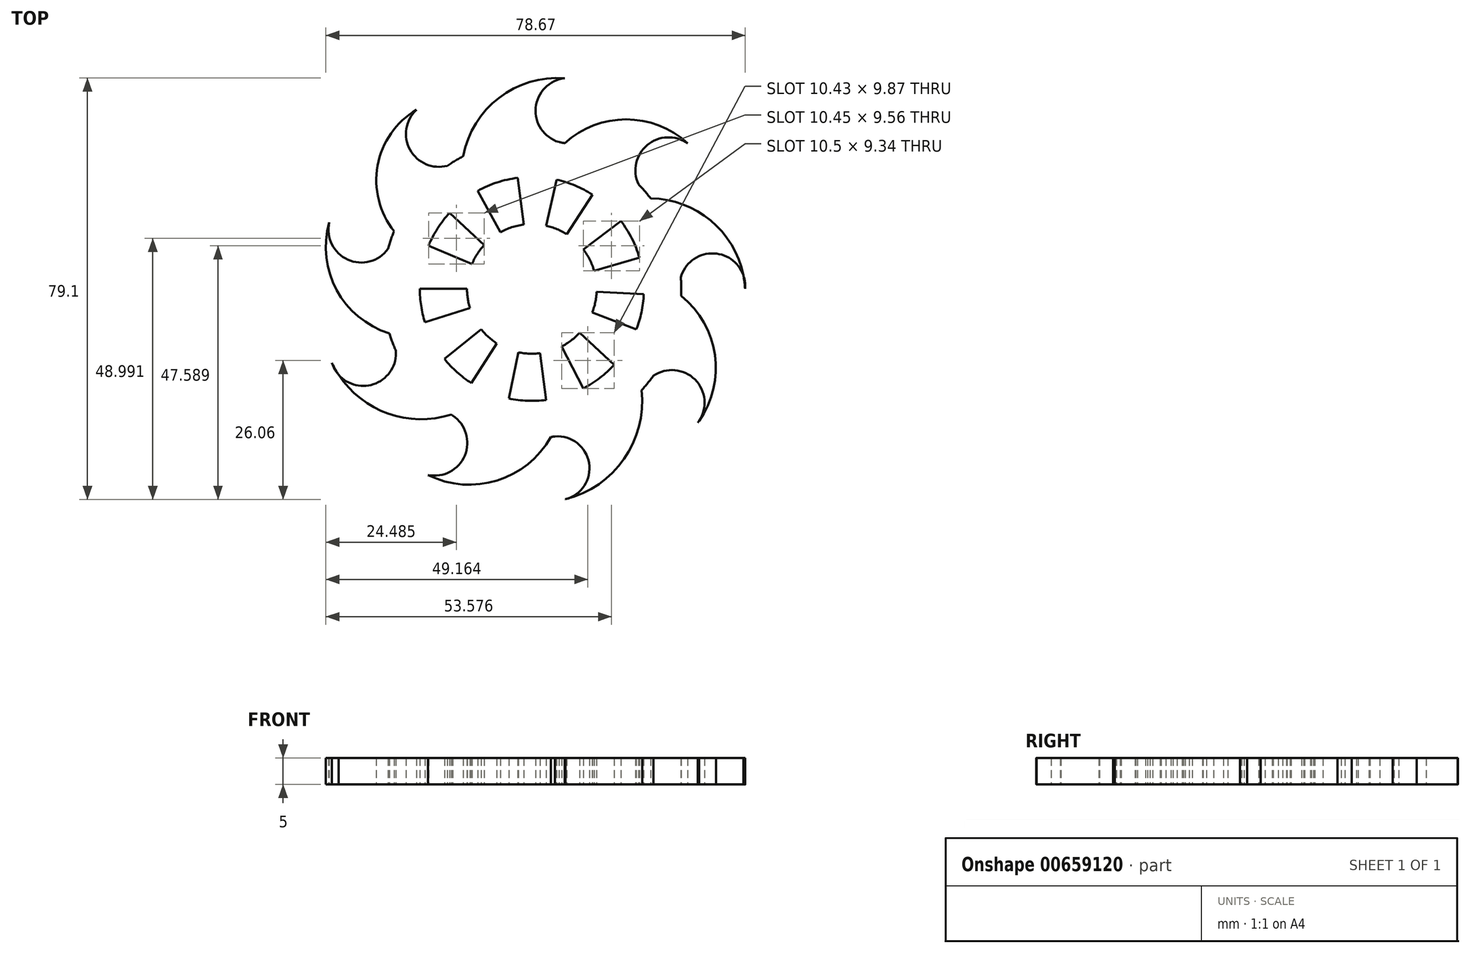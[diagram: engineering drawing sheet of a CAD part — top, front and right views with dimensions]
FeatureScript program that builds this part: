
annotation { "Feature Type Name" : "Feature", "Feature Type Description" : "" }
export const myFeature = defineFeature(function(context is Context, id is Id, definition is map)
    precondition{}
    {
        {
            var Q0;
            Q0=qCreatedBy(makeId("Top.planeOp"),FACE);
            var sketch = newSketch(context, id + "F0", { "sketchPlane" : qUnion([Q0])});
            skCircle(sketch, "E0", {"center": v(0, 0) * mm, "radius": 28.02 * mm});
            skCircle(sketch, "E1.cCircle", {"center": v(0, 0) * mm, "radius": 28.02 * mm, "construction": true});
            skLineSegment(sketch, "E1.0", {"start": v(20.6, -19) * mm, "end": v(3.57, -27.8) * mm});
            skLineSegment(sketch, "E1.1", {"start": v(3.57, -27.8) * mm, "end": v(-15.14, -23.58) * mm});
            skLineSegment(sketch, "E1.2", {"start": v(-15.14, -23.58) * mm, "end": v(-26.75, -8.34) * mm});
            skLineSegment(sketch, "E1.3", {"start": v(-26.75, -8.34) * mm, "end": v(-25.85, 10.8) * mm});
            skLineSegment(sketch, "E1.4", {"start": v(-25.85, 10.8) * mm, "end": v(-12.86, 24.9) * mm});
            skLineSegment(sketch, "E1.5", {"start": v(-12.86, 24.9) * mm, "end": v(6.16, 27.34) * mm});
            skLineSegment(sketch, "E1.6", {"start": v(6.16, 27.34) * mm, "end": v(22.29, 16.99) * mm});
            skLineSegment(sketch, "E1.7", {"start": v(22.29, 16.99) * mm, "end": v(28, -1.32) * mm});
            skLineSegment(sketch, "E1.8", {"start": v(28, -1.32) * mm, "end": v(20.6, -19) * mm});
            skLineSegment(sketch, "E2", {"start": v(6.16, 27.34) * mm, "end": v(0.33, 1.46) * mm});
            skLineSegment(sketch, "E3", {"start": v(1.2, 0.9) * mm, "end": v(22.29, 16.99) * mm});
            skLineSegment(sketch, "E4", {"start": v(1.5, -0.07) * mm, "end": v(28, -1.32) * mm});
            skLineSegment(sketch, "E5", {"start": v(1.1, -1.02) * mm, "end": v(20.6, -19) * mm});
            skLineSegment(sketch, "E6", {"start": v(0.2, -1.49) * mm, "end": v(3.57, -27.8) * mm});
            skLineSegment(sketch, "E7", {"start": v(-0.81, -1.26) * mm, "end": v(-15.14, -23.58) * mm});
            skLineSegment(sketch, "E8", {"start": v(-1.43, -0.45) * mm, "end": v(-26.75, -8.34) * mm});
            skLineSegment(sketch, "E9", {"start": v(-1.38, 0.58) * mm, "end": v(-25.85, 10.8) * mm});
            skLineSegment(sketch, "E10", {"start": v(-0.73, 1.31) * mm, "end": v(-13.44, 24.27) * mm});
            skArc(sketch, "E11", {"start": v(-21.68, 33.62) * mm, "mid": v(-22.37, 33.16) * mm, "end": v(-23.06, 32.69) * mm});
            skArc(sketch, "E12", {"start": v(29.2, 27.34) * mm, "mid": v(17.68, 31.81) * mm, "end": v(6.16, 27.34) * mm});
            skArc(sketch, "E13", {"start": v(29.2, 27.34) * mm, "mid": v(20.47, 25.68) * mm, "end": v(22.29, 16.99) * mm});
            skArc(sketch, "E14", {"start": v(40, 0) * mm, "mid": v(34.5, 11.98) * mm, "end": v(22.29, 16.99) * mm});
            skArc(sketch, "E15", {"start": v(40, 0) * mm, "mid": v(33.2, 6.63) * mm, "end": v(28, -1.32) * mm});
            skArc(sketch, "E16", {"start": v(31.11, -25.14) * mm, "mid": v(34.38, -12.6) * mm, "end": v(28, -1.32) * mm});
            skArc(sketch, "E17", {"start": v(31.11, -25.14) * mm, "mid": v(29.36, -16.07) * mm, "end": v(20.6, -19) * mm});
            skArc(sketch, "E18", {"start": v(6.16, -39.52) * mm, "mid": v(17.24, -31.98) * mm, "end": v(20.6, -19) * mm});
            skArc(sketch, "E19", {"start": v(6.16, -39.52) * mm, "mid": v(10.65, -32.38) * mm, "end": v(3.57, -27.8) * mm});
            skArc(sketch, "E20", {"start": v(-19.49, -34.93) * mm, "mid": v(-6.54, -35.97) * mm, "end": v(3.57, -27.8) * mm});
            skArc(sketch, "E21", {"start": v(-19.49, -34.93) * mm, "mid": v(-12.52, -31.1) * mm, "end": v(-15.14, -23.58) * mm});
            skArc(sketch, "E22", {"start": v(-37.5, -13.9) * mm, "mid": v(-28.14, -22.95) * mm, "end": v(-15.14, -23.58) * mm});
            skPoint(sketch, "E22.startSnap0", {"position": v(1.78, -13.9) * mm});
            skArc(sketch, "E23", {"start": v(-37.5, -13.9) * mm, "mid": v(-28.82, -17.52) * mm, "end": v(-26.75, -8.34) * mm});
            skArc(sketch, "E24", {"start": v(-38.01, 12.46) * mm, "mid": v(-36.61, -0.23) * mm, "end": v(-26.75, -8.34) * mm});
            skArc(sketch, "E25", {"start": v(-38.01, 12.46) * mm, "mid": v(-32.83, 5) * mm, "end": v(-25.85, 10.8) * mm});
            skArc(sketch, "E26", {"start": v(-21.68, 33.62) * mm, "mid": v(-28.93, 23.16) * mm, "end": v(-25.85, 10.8) * mm});
            skArc(sketch, "E27", {"start": v(-21.68, 33.62) * mm, "mid": v(-21.78, 24.7) * mm, "end": v(-12.86, 24.9) * mm});
            skArc(sketch, "E28", {"start": v(6.16, 39.52) * mm, "mid": v(-6.17, 35.87) * mm, "end": v(-12.86, 24.9) * mm});
            skArc(sketch, "E29", {"start": v(6.16, 39.52) * mm, "mid": v(0.7, 33.43) * mm, "end": v(6.16, 27.34) * mm});
            skArc(sketch, "E30.trimOffspring", {"start": v(-37.5, -13.9) * mm, "mid": v(-37.38, -14.25) * mm, "end": v(-37.24, -14.6) * mm});
            skArc(sketch, "E31.trimOffspring", {"start": v(40, 0) * mm, "mid": v(40, 0.6) * mm, "end": v(39.98, 1.22) * mm});
            skCircle(sketch, "E32", {"center": v(0, 0) * mm, "radius": 1.5 * mm});
            skLineSegment(sketch, "E33", {"start": v(0, 0) * mm, "end": v(-3.57, 27.8) * mm});
            skLineSegment(sketch, "E34", {"start": v(-3.57, 27.8) * mm, "end": v(0, 0) * mm});
            skLineSegment(sketch, "E35", {"start": v(0, 0) * mm, "end": v(15.14, 23.58) * mm});
            skLineSegment(sketch, "E36", {"start": v(15.14, 23.58) * mm, "end": v(0, 0) * mm});
            skLineSegment(sketch, "E37", {"start": v(0, 0) * mm, "end": v(26.9, 7.83) * mm});
            skPoint(sketch, "E37.endSnap0", {"position": v(25.14, 7.83) * mm});
            skLineSegment(sketch, "E38", {"start": v(26.9, 7.83) * mm, "end": v(0, 0) * mm});
            skLineSegment(sketch, "E39", {"start": v(0, 0) * mm, "end": v(26.12, -10.16) * mm});
            skPoint(sketch, "E39.endSnap0", {"position": v(24.3, -10.16) * mm});
            skLineSegment(sketch, "E40", {"start": v(26.12, -10.16) * mm, "end": v(0, 0) * mm});
            skLineSegment(sketch, "E41", {"start": v(0, 0) * mm, "end": v(12.86, -24.9) * mm});
            skLineSegment(sketch, "E42", {"start": v(12.86, -24.9) * mm, "end": v(0, 0) * mm});
            skLineSegment(sketch, "E43", {"start": v(0, 0) * mm, "end": v(-5.78, -27.42) * mm});
            skPoint(sketch, "E43.endSnap0", {"position": v(-5.78, -25.69) * mm});
            skLineSegment(sketch, "E44", {"start": v(-5.78, -27.42) * mm, "end": v(0, 0) * mm});
            skLineSegment(sketch, "E45", {"start": v(0, 0) * mm, "end": v(-21.87, -17.52) * mm});
            skLineSegment(sketch, "E46", {"start": v(-21.87, -17.52) * mm, "end": v(0, 0) * mm});
            skLineSegment(sketch, "E47", {"start": v(0, 0) * mm, "end": v(-28.02, 0) * mm});
            skLineSegment(sketch, "E48", {"start": v(-28.02, 0) * mm, "end": v(0, 0) * mm});
            skLineSegment(sketch, "E49", {"start": v(0, 0) * mm, "end": v(-20.6, 19) * mm});
            skLineSegment(sketch, "E50", {"start": v(-20.6, 19) * mm, "end": v(0, 0) * mm});
            skCircle(sketch, "E51", {"center": v(0, 0) * mm, "radius": 21.02 * mm});
            skCircle(sketch, "E52", {"center": v(0, 0) * mm, "radius": 12.16 * mm});
            skLineSegment(sketch, "E53", {"start": v(-0.73, 1.31) * mm, "end": v(0, 0) * mm});
            skLineSegment(sketch, "E54", {"start": v(0.33, 1.46) * mm, "end": v(0, 0) * mm});
            skLineSegment(sketch, "E55", {"start": v(1.2, 0.9) * mm, "end": v(0, 0) * mm});
            skLineSegment(sketch, "E56", {"start": v(-1.38, 0.58) * mm, "end": v(0, 0) * mm});
            skLineSegment(sketch, "E57", {"start": v(-1.43, -0.45) * mm, "end": v(0, 0) * mm});
            skLineSegment(sketch, "E58", {"start": v(-0.81, -1.26) * mm, "end": v(0, 0) * mm});
            skLineSegment(sketch, "E59", {"start": v(0.2, -1.49) * mm, "end": v(0, 0) * mm});
            skLineSegment(sketch, "E60", {"start": v(1.1, -1.02) * mm, "end": v(0, 0) * mm});
            skLineSegment(sketch, "E61", {"start": v(1.5, -0.07) * mm, "end": v(0, 0) * mm});
            skSolve(sketch);
        }
        {
            var Q0;
            Q0 = qSketchRegion(id + "F0", true);
            var Q1;
            {var subQ0=sQuery(id+"F0.wireOp",EDGE,"E32");var subQ4=makeQuery(id+"F0.imprint","INTERSECT",VERTEX,{"derivedFrom":[sQuery(id+"F0.wireOp",EDGE,"E2"),subQ0]});Q1=makeQuery(id+"F0.imprint","IMPRINT",FACE,{"disambiguationData":[TD([[makeQuery(id+"F0.imprint","IMPRINT",EDGE,{"disambiguationData":[TD([[subQ4,1.0]])],"derivedFrom":subQ0}),1.0]])]});}
            var Q2;
            {var subQ0=sQuery(id+"F0.wireOp",EDGE,"E10");var subQ1=sQuery(id+"F0.wireOp",EDGE,"E1.4");var subQ2=makeQuery(id+"F0.imprint","INTERSECT",VERTEX,{"derivedFrom":[subQ1,subQ0]});Q2=makeQuery(id+"F0.imprint","IMPRINT",FACE,{"disambiguationData":[TD([[makeQuery(id+"F0.imprint","IMPRINT",EDGE,{"disambiguationData":[TD([[subQ2,1.0]])],"derivedFrom":subQ1}),-1.0]])]});}
            var Q3;
            {var subQ0=sQuery(id+"F0.wireOp",EDGE,"E32");var subQ1=sQuery(id+"F0.wireOp",EDGE,"E10");var subQ2=makeQuery(id+"F0.imprint","INTERSECT",VERTEX,{"derivedFrom":[subQ1,subQ0]});Q3=makeQuery(id+"F0.imprint","IMPRINT",FACE,{"disambiguationData":[TD([[makeQuery(id+"F0.imprint","IMPRINT",EDGE,{"disambiguationData":[TD([[subQ2,-1.0]])],"derivedFrom":subQ1}),1.0]])]});}
            var Q4;
            {var subQ0=sQuery(id+"F0.wireOp",EDGE,"E32");var subQ1=sQuery(id+"F0.wireOp",EDGE,"E9");var subQ2=makeQuery(id+"F0.imprint","INTERSECT",VERTEX,{"derivedFrom":[subQ1,subQ0]});Q4=makeQuery(id+"F0.imprint","IMPRINT",FACE,{"disambiguationData":[TD([[makeQuery(id+"F0.imprint","IMPRINT",EDGE,{"disambiguationData":[TD([[subQ2,-1.0]])],"derivedFrom":subQ1}),-1.0]])]});}
            var Q5;
            {var subQ0=sQuery(id+"F0.wireOp",EDGE,"E32");var subQ1=sQuery(id+"F0.wireOp",EDGE,"E9");var subQ2=makeQuery(id+"F0.imprint","INTERSECT",VERTEX,{"derivedFrom":[subQ1,subQ0]});Q5=makeQuery(id+"F0.imprint","IMPRINT",FACE,{"disambiguationData":[TD([[makeQuery(id+"F0.imprint","IMPRINT",EDGE,{"disambiguationData":[TD([[subQ2,-1.0]])],"derivedFrom":subQ1}),1.0]])]});}
            var Q6;
            {var subQ0=sQuery(id+"F0.wireOp",EDGE,"E32");var subQ1=sQuery(id+"F0.wireOp",EDGE,"E8");var subQ2=makeQuery(id+"F0.imprint","INTERSECT",VERTEX,{"derivedFrom":[subQ1,subQ0]});Q6=makeQuery(id+"F0.imprint","IMPRINT",FACE,{"disambiguationData":[TD([[makeQuery(id+"F0.imprint","IMPRINT",EDGE,{"disambiguationData":[TD([[subQ2,-1.0]])],"derivedFrom":subQ1}),1.0]])]});}
            var Q7;
            {var subQ0=sQuery(id+"F0.wireOp",EDGE,"E32");var subQ1=sQuery(id+"F0.wireOp",EDGE,"E8");var subQ2=makeQuery(id+"F0.imprint","INTERSECT",VERTEX,{"derivedFrom":[subQ1,subQ0]});Q7=makeQuery(id+"F0.imprint","IMPRINT",FACE,{"disambiguationData":[TD([[makeQuery(id+"F0.imprint","IMPRINT",EDGE,{"disambiguationData":[TD([[subQ2,-1.0]])],"derivedFrom":subQ1}),-1.0]])]});}
            var Q8;
            {var subQ0=sQuery(id+"F0.wireOp",EDGE,"E32");var subQ1=sQuery(id+"F0.wireOp",EDGE,"E7");var subQ2=makeQuery(id+"F0.imprint","INTERSECT",VERTEX,{"derivedFrom":[subQ1,subQ0]});Q8=makeQuery(id+"F0.imprint","IMPRINT",FACE,{"disambiguationData":[TD([[makeQuery(id+"F0.imprint","IMPRINT",EDGE,{"disambiguationData":[TD([[subQ2,-1.0]])],"derivedFrom":subQ1}),1.0]])]});}
            var Q9;
            {var subQ0=sQuery(id+"F0.wireOp",EDGE,"E32");var subQ1=sQuery(id+"F0.wireOp",EDGE,"E7");var subQ2=makeQuery(id+"F0.imprint","INTERSECT",VERTEX,{"derivedFrom":[subQ1,subQ0]});Q9=makeQuery(id+"F0.imprint","IMPRINT",FACE,{"disambiguationData":[TD([[makeQuery(id+"F0.imprint","IMPRINT",EDGE,{"disambiguationData":[TD([[subQ2,-1.0]])],"derivedFrom":subQ1}),-1.0]])]});}
            var Q10;
            {var subQ0=sQuery(id+"F0.wireOp",EDGE,"E32");var subQ1=sQuery(id+"F0.wireOp",EDGE,"E6");var subQ2=makeQuery(id+"F0.imprint","INTERSECT",VERTEX,{"derivedFrom":[subQ1,subQ0]});Q10=makeQuery(id+"F0.imprint","IMPRINT",FACE,{"disambiguationData":[TD([[makeQuery(id+"F0.imprint","IMPRINT",EDGE,{"disambiguationData":[TD([[subQ2,-1.0]])],"derivedFrom":subQ1}),1.0]])]});}
            var Q11;
            {var subQ0=sQuery(id+"F0.wireOp",EDGE,"E32");var subQ1=sQuery(id+"F0.wireOp",EDGE,"E6");var subQ2=makeQuery(id+"F0.imprint","INTERSECT",VERTEX,{"derivedFrom":[subQ1,subQ0]});Q11=makeQuery(id+"F0.imprint","IMPRINT",FACE,{"disambiguationData":[TD([[makeQuery(id+"F0.imprint","IMPRINT",EDGE,{"disambiguationData":[TD([[subQ2,-1.0]])],"derivedFrom":subQ1}),-1.0]])]});}
            var Q12;
            {var subQ0=sQuery(id+"F0.wireOp",EDGE,"E32");var subQ1=sQuery(id+"F0.wireOp",EDGE,"E5");var subQ2=makeQuery(id+"F0.imprint","INTERSECT",VERTEX,{"derivedFrom":[subQ1,subQ0]});Q12=makeQuery(id+"F0.imprint","IMPRINT",FACE,{"disambiguationData":[TD([[makeQuery(id+"F0.imprint","IMPRINT",EDGE,{"disambiguationData":[TD([[subQ2,-1.0]])],"derivedFrom":subQ1}),-1.0]])]});}
            var Q13;
            {var subQ0=sQuery(id+"F0.wireOp",EDGE,"E32");var subQ1=sQuery(id+"F0.wireOp",EDGE,"E5");var subQ2=makeQuery(id+"F0.imprint","INTERSECT",VERTEX,{"derivedFrom":[subQ1,subQ0]});Q13=makeQuery(id+"F0.imprint","IMPRINT",FACE,{"disambiguationData":[TD([[makeQuery(id+"F0.imprint","IMPRINT",EDGE,{"disambiguationData":[TD([[subQ2,-1.0]])],"derivedFrom":subQ1}),1.0]])]});}
            var Q14;
            {var subQ0=sQuery(id+"F0.wireOp",EDGE,"E32");var subQ1=sQuery(id+"F0.wireOp",EDGE,"E4");var subQ2=makeQuery(id+"F0.imprint","INTERSECT",VERTEX,{"derivedFrom":[subQ1,subQ0]});Q14=makeQuery(id+"F0.imprint","IMPRINT",FACE,{"disambiguationData":[TD([[makeQuery(id+"F0.imprint","IMPRINT",EDGE,{"disambiguationData":[TD([[subQ2,-1.0]])],"derivedFrom":subQ1}),-1.0]])]});}
            var Q15;
            {var subQ0=sQuery(id+"F0.wireOp",EDGE,"E32");var subQ1=sQuery(id+"F0.wireOp",EDGE,"E4");var subQ2=makeQuery(id+"F0.imprint","INTERSECT",VERTEX,{"derivedFrom":[subQ1,subQ0]});Q15=makeQuery(id+"F0.imprint","IMPRINT",FACE,{"disambiguationData":[TD([[makeQuery(id+"F0.imprint","IMPRINT",EDGE,{"disambiguationData":[TD([[subQ2,-1.0]])],"derivedFrom":subQ1}),1.0]])]});}
            var Q16;
            {var subQ0=sQuery(id+"F0.wireOp",EDGE,"E32");var subQ1=sQuery(id+"F0.wireOp",EDGE,"E3");var subQ2=makeQuery(id+"F0.imprint","INTERSECT",VERTEX,{"derivedFrom":[subQ1,subQ0]});Q16=makeQuery(id+"F0.imprint","IMPRINT",FACE,{"disambiguationData":[TD([[makeQuery(id+"F0.imprint","IMPRINT",EDGE,{"disambiguationData":[TD([[subQ2,-1.0]])],"derivedFrom":subQ1}),-1.0]])]});}
            var Q17;
            {var subQ0=sQuery(id+"F0.wireOp",EDGE,"E32");var subQ1=sQuery(id+"F0.wireOp",EDGE,"E3");var subQ2=makeQuery(id+"F0.imprint","INTERSECT",VERTEX,{"derivedFrom":[subQ1,subQ0]});Q17=makeQuery(id+"F0.imprint","IMPRINT",FACE,{"disambiguationData":[TD([[makeQuery(id+"F0.imprint","IMPRINT",EDGE,{"disambiguationData":[TD([[subQ2,-1.0]])],"derivedFrom":subQ1}),1.0]])]});}
            var Q18;
            {var subQ0=sQuery(id+"F0.wireOp",EDGE,"E32");var subQ1=sQuery(id+"F0.wireOp",EDGE,"E2");var subQ2=makeQuery(id+"F0.imprint","INTERSECT",VERTEX,{"derivedFrom":[subQ1,subQ0]});Q18=makeQuery(id+"F0.imprint","IMPRINT",FACE,{"disambiguationData":[TD([[makeQuery(id+"F0.imprint","IMPRINT",EDGE,{"disambiguationData":[TD([[subQ2,1.0]])],"derivedFrom":subQ1}),1.0]])]});}
            var Q19;
            {var subQ0=sQuery(id+"F0.wireOp",EDGE,"E32");var subQ1=sQuery(id+"F0.wireOp",EDGE,"E2");var subQ2=makeQuery(id+"F0.imprint","INTERSECT",VERTEX,{"derivedFrom":[subQ1,subQ0]});Q19=makeQuery(id+"F0.imprint","IMPRINT",FACE,{"disambiguationData":[TD([[makeQuery(id+"F0.imprint","IMPRINT",EDGE,{"disambiguationData":[TD([[subQ2,1.0]])],"derivedFrom":subQ1}),-1.0]])]});}
            var Q20;
            {var subQ0=sQuery(id+"F0.wireOp",EDGE,"E32");var subQ1=sQuery(id+"F0.wireOp",EDGE,"E10");var subQ2=makeQuery(id+"F0.imprint","INTERSECT",VERTEX,{"derivedFrom":[subQ1,subQ0]});Q20=makeQuery(id+"F0.imprint","IMPRINT",FACE,{"disambiguationData":[TD([[makeQuery(id+"F0.imprint","IMPRINT",EDGE,{"disambiguationData":[TD([[subQ2,-1.0]])],"derivedFrom":subQ1}),-1.0]])]});}
            var Q21;
            {var subQ0=sQuery(id+"F0.wireOp",EDGE,"E51");var subQ1=sQuery(id+"F0.wireOp",EDGE,"E2");var subQ2=makeQuery(id+"F0.imprint","INTERSECT",VERTEX,{"derivedFrom":[subQ1,subQ0]});Q21=makeQuery(id+"F0.imprint","IMPRINT",FACE,{"disambiguationData":[TD([[makeQuery(id+"F0.imprint","IMPRINT",EDGE,{"disambiguationData":[TD([[subQ2,-1.0]])],"derivedFrom":subQ1}),-1.0]])]});}
            var Q22;
            {var subQ0=sQuery(id+"F0.wireOp",EDGE,"E52");var subQ1=sQuery(id+"F0.wireOp",EDGE,"E3");var subQ2=makeQuery(id+"F0.imprint","INTERSECT",VERTEX,{"derivedFrom":[subQ1,subQ0]});Q22=makeQuery(id+"F0.imprint","IMPRINT",FACE,{"disambiguationData":[TD([[makeQuery(id+"F0.imprint","IMPRINT",EDGE,{"disambiguationData":[TD([[subQ2,-1.0]])],"derivedFrom":subQ1}),1.0]])]});}
            var Q23;
            {var subQ0=sQuery(id+"F0.wireOp",EDGE,"E52");var subQ1=sQuery(id+"F0.wireOp",EDGE,"E4");var subQ2=makeQuery(id+"F0.imprint","INTERSECT",VERTEX,{"derivedFrom":[subQ1,subQ0]});Q23=makeQuery(id+"F0.imprint","IMPRINT",FACE,{"disambiguationData":[TD([[makeQuery(id+"F0.imprint","IMPRINT",EDGE,{"disambiguationData":[TD([[subQ2,-1.0]])],"derivedFrom":subQ1}),1.0]])]});}
            var Q24;
            {var subQ0=sQuery(id+"F0.wireOp",EDGE,"E52");var subQ1=sQuery(id+"F0.wireOp",EDGE,"E6");var subQ2=makeQuery(id+"F0.imprint","INTERSECT",VERTEX,{"derivedFrom":[subQ1,subQ0]});Q24=makeQuery(id+"F0.imprint","IMPRINT",FACE,{"disambiguationData":[TD([[makeQuery(id+"F0.imprint","IMPRINT",EDGE,{"disambiguationData":[TD([[subQ2,-1.0]])],"derivedFrom":subQ1}),1.0]])]});}
            var Q25;
            {var subQ0=sQuery(id+"F0.wireOp",EDGE,"E52");var subQ1=sQuery(id+"F0.wireOp",EDGE,"E7");var subQ2=makeQuery(id+"F0.imprint","INTERSECT",VERTEX,{"derivedFrom":[subQ1,subQ0]});Q25=makeQuery(id+"F0.imprint","IMPRINT",FACE,{"disambiguationData":[TD([[makeQuery(id+"F0.imprint","IMPRINT",EDGE,{"disambiguationData":[TD([[subQ2,-1.0]])],"derivedFrom":subQ1}),1.0]])]});}
            var Q26;
            {var subQ0=sQuery(id+"F0.wireOp",EDGE,"E52");var subQ1=sQuery(id+"F0.wireOp",EDGE,"E8");var subQ2=makeQuery(id+"F0.imprint","INTERSECT",VERTEX,{"derivedFrom":[subQ1,subQ0]});Q26=makeQuery(id+"F0.imprint","IMPRINT",FACE,{"disambiguationData":[TD([[makeQuery(id+"F0.imprint","IMPRINT",EDGE,{"disambiguationData":[TD([[subQ2,-1.0]])],"derivedFrom":subQ1}),1.0]])]});}
            var Q27;
            {var subQ0=sQuery(id+"F0.wireOp",EDGE,"E52");var subQ1=sQuery(id+"F0.wireOp",EDGE,"E9");var subQ2=makeQuery(id+"F0.imprint","INTERSECT",VERTEX,{"derivedFrom":[subQ1,subQ0]});Q27=makeQuery(id+"F0.imprint","IMPRINT",FACE,{"disambiguationData":[TD([[makeQuery(id+"F0.imprint","IMPRINT",EDGE,{"disambiguationData":[TD([[subQ2,-1.0]])],"derivedFrom":subQ1}),1.0]])]});}
            var Q28;
            {var subQ0=sQuery(id+"F0.wireOp",EDGE,"E52");var subQ1=sQuery(id+"F0.wireOp",EDGE,"E10");var subQ2=makeQuery(id+"F0.imprint","INTERSECT",VERTEX,{"derivedFrom":[subQ1,subQ0]});Q28=makeQuery(id+"F0.imprint","IMPRINT",FACE,{"disambiguationData":[TD([[makeQuery(id+"F0.imprint","IMPRINT",EDGE,{"disambiguationData":[TD([[subQ2,-1.0]])],"derivedFrom":subQ1}),1.0]])]});}
            var Q29;
            {var subQ0=sQuery(id+"F0.wireOp",EDGE,"E52");var subQ1=sQuery(id+"F0.wireOp",EDGE,"E5");var subQ2=makeQuery(id+"F0.imprint","INTERSECT",VERTEX,{"derivedFrom":[subQ1,subQ0]});Q29=makeQuery(id+"F0.imprint","IMPRINT",FACE,{"disambiguationData":[TD([[makeQuery(id+"F0.imprint","IMPRINT",EDGE,{"disambiguationData":[TD([[subQ2,-1.0]])],"derivedFrom":subQ1}),1.0]])]});}
            var Q30;
            {var subQ0=sQuery(id+"F0.wireOp",EDGE,"E32");var subQ1=makeQuery(id+"F0.imprint","INTERSECT",VERTEX,{"derivedFrom":[sQuery(id+"F0.wireOp",EDGE,"E9"),subQ0]});Q30=makeQuery(id+"F0.imprint","IMPRINT",FACE,{"disambiguationData":[TD([[makeQuery(id+"F0.imprint","IMPRINT",EDGE,{"disambiguationData":[TD([[subQ1,1.0]])],"derivedFrom":subQ0}),1.0]])]});}
            var Q31;
            {var subQ0=sQuery(id+"F0.wireOp",EDGE,"E32");var subQ1=makeQuery(id+"F0.imprint","INTERSECT",VERTEX,{"derivedFrom":[sQuery(id+"F0.wireOp",EDGE,"E10"),subQ0]});Q31=makeQuery(id+"F0.imprint","IMPRINT",FACE,{"disambiguationData":[TD([[makeQuery(id+"F0.imprint","IMPRINT",EDGE,{"disambiguationData":[TD([[subQ1,1.0]])],"derivedFrom":subQ0}),1.0]])]});}
            var Q32;
            {var subQ0=sQuery(id+"F0.wireOp",EDGE,"E32");var subQ1=makeQuery(id+"F0.imprint","INTERSECT",VERTEX,{"derivedFrom":[sQuery(id+"F0.wireOp",EDGE,"E8"),subQ0]});Q32=makeQuery(id+"F0.imprint","IMPRINT",FACE,{"disambiguationData":[TD([[makeQuery(id+"F0.imprint","IMPRINT",EDGE,{"disambiguationData":[TD([[subQ1,1.0]])],"derivedFrom":subQ0}),1.0]])]});}
            var Q33;
            {var subQ0=sQuery(id+"F0.wireOp",EDGE,"E32");var subQ1=makeQuery(id+"F0.imprint","INTERSECT",VERTEX,{"derivedFrom":[sQuery(id+"F0.wireOp",EDGE,"E7"),subQ0]});Q33=makeQuery(id+"F0.imprint","IMPRINT",FACE,{"disambiguationData":[TD([[makeQuery(id+"F0.imprint","IMPRINT",EDGE,{"disambiguationData":[TD([[subQ1,1.0]])],"derivedFrom":subQ0}),1.0]])]});}
            var Q34;
            {var subQ0=sQuery(id+"F0.wireOp",EDGE,"E32");var subQ1=makeQuery(id+"F0.imprint","INTERSECT",VERTEX,{"derivedFrom":[sQuery(id+"F0.wireOp",EDGE,"E6"),subQ0]});Q34=makeQuery(id+"F0.imprint","IMPRINT",FACE,{"disambiguationData":[TD([[makeQuery(id+"F0.imprint","IMPRINT",EDGE,{"disambiguationData":[TD([[subQ1,1.0]])],"derivedFrom":subQ0}),1.0]])]});}
            var Q35;
            {var subQ0=sQuery(id+"F0.wireOp",EDGE,"E32");var subQ1=makeQuery(id+"F0.imprint","INTERSECT",VERTEX,{"derivedFrom":[sQuery(id+"F0.wireOp",EDGE,"E5"),subQ0]});Q35=makeQuery(id+"F0.imprint","IMPRINT",FACE,{"disambiguationData":[TD([[makeQuery(id+"F0.imprint","IMPRINT",EDGE,{"disambiguationData":[TD([[subQ1,1.0]])],"derivedFrom":subQ0}),1.0]])]});}
            var Q36;
            {var subQ0=sQuery(id+"F0.wireOp",EDGE,"E32");var subQ1=makeQuery(id+"F0.imprint","INTERSECT",VERTEX,{"derivedFrom":[sQuery(id+"F0.wireOp",EDGE,"E4"),subQ0]});Q36=makeQuery(id+"F0.imprint","IMPRINT",FACE,{"disambiguationData":[TD([[makeQuery(id+"F0.imprint","IMPRINT",EDGE,{"disambiguationData":[TD([[subQ1,1.0]])],"derivedFrom":subQ0}),1.0]])]});}
            var Q37;
            {var subQ0=sQuery(id+"F0.wireOp",EDGE,"E32");var subQ1=makeQuery(id+"F0.imprint","INTERSECT",VERTEX,{"derivedFrom":[sQuery(id+"F0.wireOp",EDGE,"E3"),subQ0]});Q37=makeQuery(id+"F0.imprint","IMPRINT",FACE,{"disambiguationData":[TD([[makeQuery(id+"F0.imprint","IMPRINT",EDGE,{"disambiguationData":[TD([[subQ1,1.0]])],"derivedFrom":subQ0}),1.0]])]});}
            var Q38;
            {var subQ0=sQuery(id+"F0.wireOp",EDGE,"E53");Q38=makeQuery(id+"F0.imprint","IMPRINT",FACE,{"disambiguationData":[TD([[makeQuery(id+"F0.imprint","IMPRINT",EDGE,{"derivedFrom":subQ0}),-1.0]])]});}
            var Q39;
            {var subQ0=sQuery(id+"F0.wireOp",EDGE,"E56");Q39=makeQuery(id+"F0.imprint","IMPRINT",FACE,{"disambiguationData":[TD([[makeQuery(id+"F0.imprint","IMPRINT",EDGE,{"derivedFrom":subQ0}),-1.0]])]});}
            var Q40;
            {var subQ0=sQuery(id+"F0.wireOp",EDGE,"E60");Q40=makeQuery(id+"F0.imprint","IMPRINT",FACE,{"disambiguationData":[TD([[makeQuery(id+"F0.imprint","IMPRINT",EDGE,{"derivedFrom":subQ0}),-1.0]])]});}
            var Q41;
            {var subQ0=sQuery(id+"F0.wireOp",EDGE,"E59");Q41=makeQuery(id+"F0.imprint","IMPRINT",FACE,{"disambiguationData":[TD([[makeQuery(id+"F0.imprint","IMPRINT",EDGE,{"derivedFrom":subQ0}),-1.0]])]});}
            var Q42;
            {var subQ0=sQuery(id+"F0.wireOp",EDGE,"E58");Q42=makeQuery(id+"F0.imprint","IMPRINT",FACE,{"disambiguationData":[TD([[makeQuery(id+"F0.imprint","IMPRINT",EDGE,{"derivedFrom":subQ0}),-1.0]])]});}
            var Q43;
            {var subQ0=sQuery(id+"F0.wireOp",EDGE,"E57");Q43=makeQuery(id+"F0.imprint","IMPRINT",FACE,{"disambiguationData":[TD([[makeQuery(id+"F0.imprint","IMPRINT",EDGE,{"derivedFrom":subQ0}),-1.0]])]});}
            var Q44;
            {var subQ0=sQuery(id+"F0.wireOp",EDGE,"E61");Q44=makeQuery(id+"F0.imprint","IMPRINT",FACE,{"disambiguationData":[TD([[makeQuery(id+"F0.imprint","IMPRINT",EDGE,{"derivedFrom":subQ0}),-1.0]])]});}
            var Q45;
            {var subQ0=sQuery(id+"F0.wireOp",EDGE,"E55");Q45=makeQuery(id+"F0.imprint","IMPRINT",FACE,{"disambiguationData":[TD([[makeQuery(id+"F0.imprint","IMPRINT",EDGE,{"derivedFrom":subQ0}),-1.0]])]});}
            var Q46;
            {var subQ0=sQuery(id+"F0.wireOp",EDGE,"E54");Q46=makeQuery(id+"F0.imprint","IMPRINT",FACE,{"disambiguationData":[TD([[makeQuery(id+"F0.imprint","IMPRINT",EDGE,{"derivedFrom":subQ0}),-1.0]])]});}
            extrude(context, id + "F1", {"entities" : qUnion([Q0, Q1, Q2, Q3, Q4, Q5, Q6, Q7, Q8, Q9, Q10, Q11, Q12, Q13, Q14, Q15, Q16, Q17, Q18, Q19, Q20, Q21, Q22, Q23, Q24, Q25, Q26, Q27, Q28, Q29, Q30, Q31, Q32, Q33, Q34, Q35, Q36, Q37, Q38, Q39, Q40, Q41, Q42, Q43, Q44, Q45, Q46]), "depth" : 5 * mm, "offsetDistance" : 25 * mm});
        }
    });
